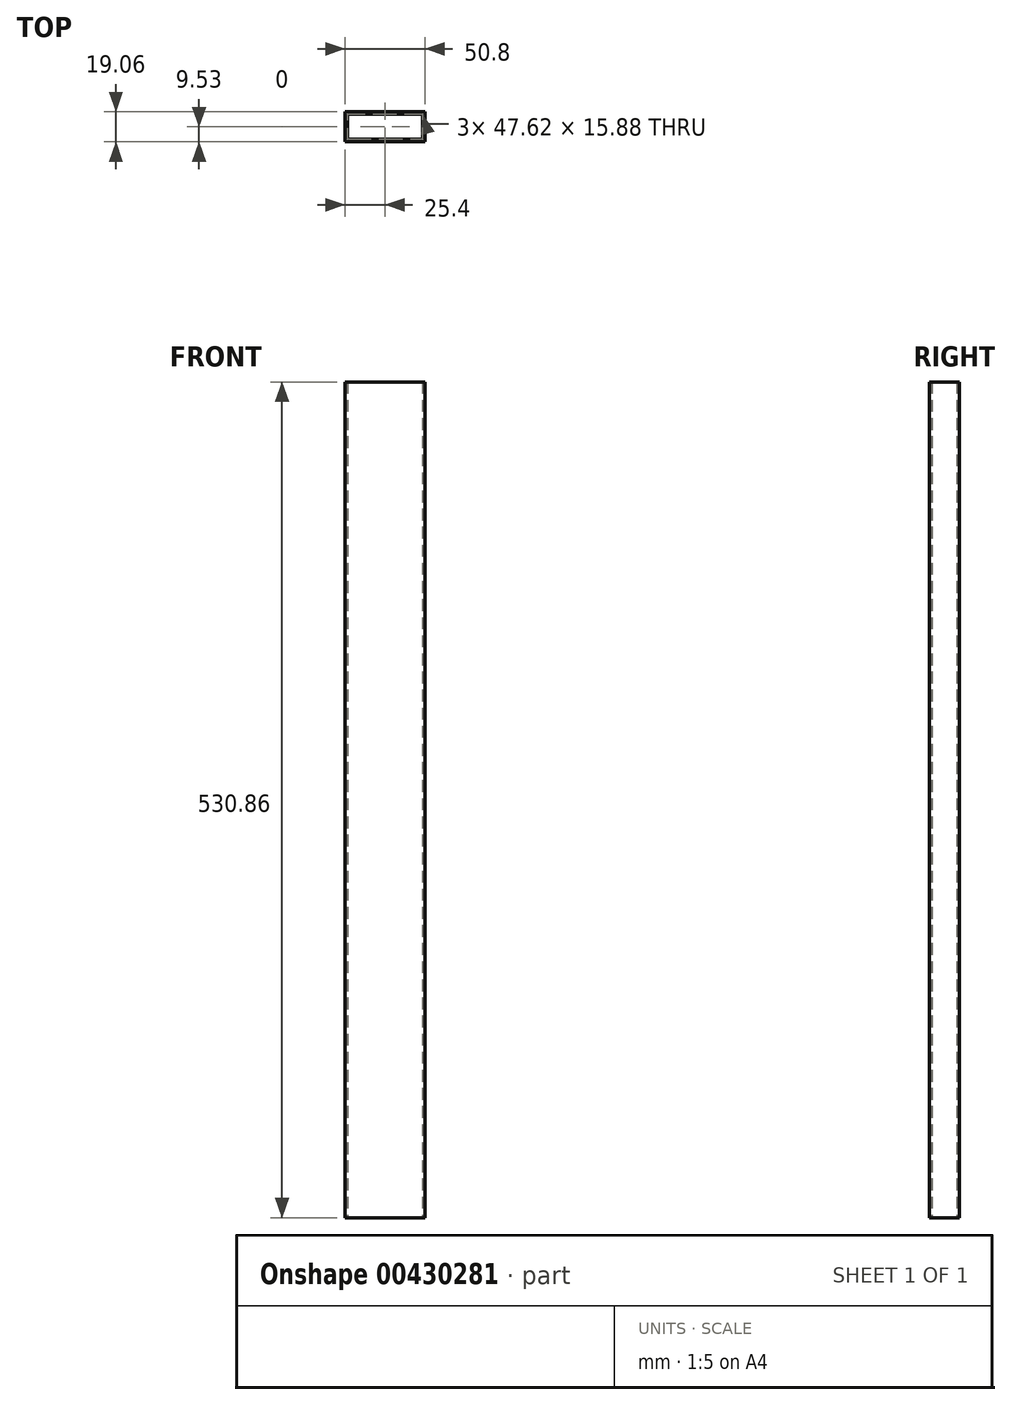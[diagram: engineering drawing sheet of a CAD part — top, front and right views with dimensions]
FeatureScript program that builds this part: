
annotation { "Feature Type Name" : "Feature", "Feature Type Description" : "" }
export const myFeature = defineFeature(function(context is Context, id is Id, definition is map)
    precondition{}
    {
        {
            var Q0;
            Q0=qCreatedBy(makeId("Top.planeOp"),FACE);
            var sketch = newSketch(context, id + "F0", { "sketchPlane" : qUnion([Q0])});
            skLineSegment(sketch, "E0.bottom", {"start": v(-25.4, 9.53) * mm, "end": v(25.4, 9.52) * mm});
            skLineSegment(sketch, "E0.top", {"start": v(-25.4, -9.52) * mm, "end": v(25.4, -9.53) * mm});
            skLineSegment(sketch, "E0.left", {"start": v(-25.4, 9.52) * mm, "end": v(-25.4, -9.52) * mm});
            skLineSegment(sketch, "E0.right", {"start": v(25.4, 9.52) * mm, "end": v(25.4, -9.52) * mm});
            skLineSegment(sketch, "E1.bottom", {"start": v(-23.81, 7.94) * mm, "end": v(23.81, 7.94) * mm});
            skLineSegment(sketch, "E1.top", {"start": v(-23.81, -7.94) * mm, "end": v(23.81, -7.94) * mm});
            skLineSegment(sketch, "E1.left", {"start": v(-23.81, 7.94) * mm, "end": v(-23.81, -7.94) * mm});
            skLineSegment(sketch, "E1.right", {"start": v(23.81, 7.94) * mm, "end": v(23.81, -7.94) * mm});
            skSolve(sketch);
        }
        {
            var Q0;
            Q0 = qSketchRegion(id + "F0", true);
            extrude(context, id + "F1", {"entities" : qUnion([Q0]), "depth" : 530.86 * mm});
        }
    });
